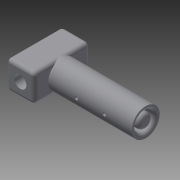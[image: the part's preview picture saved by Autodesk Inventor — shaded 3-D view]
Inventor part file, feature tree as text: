
AUTODESK INVENTOR PART (.ipt)
format: ipt  version: 2014 (Build 180170000, 170)  size: 458,240 bytes
history: native  units: mm
features: fillet x5, sketch x5, extrude x4, emboss x1
ambient origin geometry x8: Origin, YZ Plane, XZ Plane, XY Plane, X Axis, Y Axis, Z Axis, Center Point
bodies: Solid1 (feature_tree)
feature tree (15):
  extrude  "Extrusion1"  Depth=50.8mm
  extrude  "Extrusion2"  Depth=25.4mm
  extrude  "Extrusion3"  Depth=34.0868mm
  fillet  "Fillet3"  Radius=25.3238mm
  fillet  "Fillet4"  Radius=152.4mm
  fillet  "Fillet5"  Radius=22.0472mm
  fillet  "Fillet6"  Radius=152.4mm
  extrude  "Extrusion4"  Depth=6.35mm
  fillet  "Fillet7"  Radius=6.35mm
  emboss  "Emboss1"
  sketch  "Sketch1"  dims[d0=203.2mm d1=50.8mm]
  sketch  "Sketch2"  dims[d2=50.8mm d3=25.4mm]
  sketch  "Sketch3"  dims[d4=50.8mm d5=0.0mm d6=34.0868mm d7=25.3238mm d8=152.4mm d9=0.0mm d10=22.0472mm d11=152.4mm d12=0.0mm]
  sketch  "Sketch4"  dims[d15=6.35mm d16=6.35mm d17=6.35mm]
  sketch  "Sketch5"  dims[d18=6.35mm d19=6.604mm d20=50.8mm d21=101.6mm d22=152.4mm d23=0.0mm d24=25.4mm d25=13.0mm d26=2.0mm d27=0.0mm]
